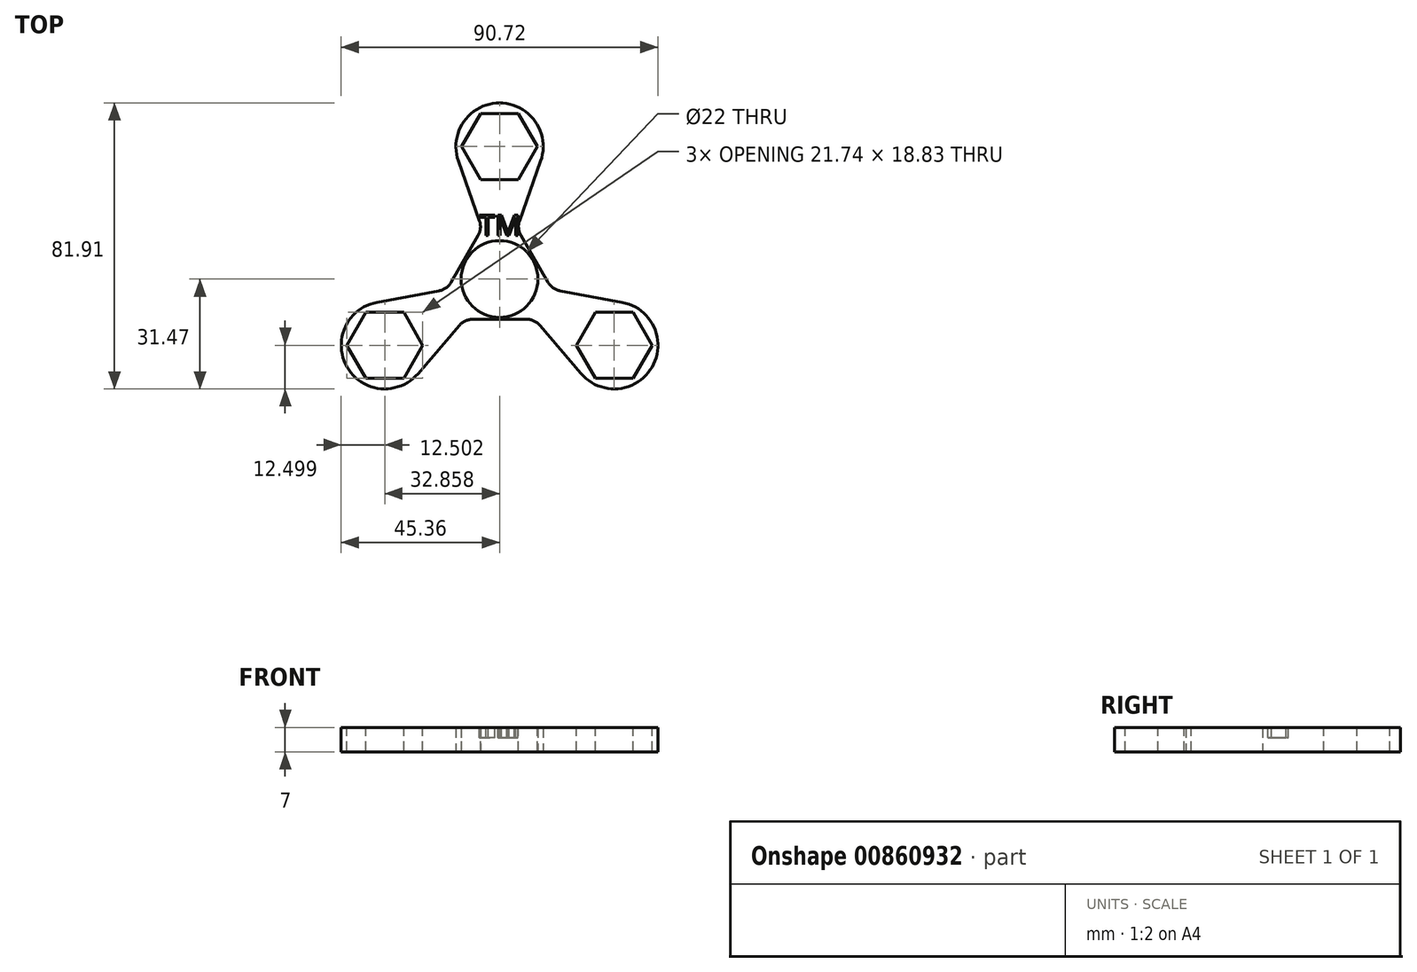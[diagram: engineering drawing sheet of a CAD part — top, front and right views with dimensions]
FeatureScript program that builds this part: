
annotation { "Feature Type Name" : "Feature", "Feature Type Description" : "" }
export const myFeature = defineFeature(function(context is Context, id is Id, definition is map)
    precondition{}
    {
        {
            var Q0;
            Q0=qCreatedBy(makeId("Top.planeOp"),FACE);
            var sketch = newSketch(context, id + "F0", { "sketchPlane" : qUnion([Q0])});
            skCircle(sketch, "E0", {"center": v(0, 0) * mm, "radius": 11 * mm});
            skArc(sketch, "E1", {"start": v(11.78, 33.76) * mm, "mid": v(0.01, 50.44) * mm, "end": v(-11.79, 33.78) * mm});
            skLineSegment(sketch, "E2", {"start": v(-11.79, 33.78) * mm, "end": v(-4.99, 14.5) * mm});
            skLineSegment(sketch, "E3", {"start": v(-4.99, 14.5) * mm, "end": v(-4.99, 14.5) * mm});
            skLineSegment(sketch, "E4", {"start": v(11.78, 33.76) * mm, "end": v(4.94, 14.5) * mm});
            skLineSegment(sketch, "E5", {"start": v(4.94, 14.5) * mm, "end": v(14.88, -2.63) * mm});
            skArc(sketch, "E6.1.0", {"start": v(-35.13, -6.68) * mm, "mid": v(-43.69, -25.2) * mm, "end": v(-23.36, -27.1) * mm});
            skLineSegment(sketch, "E6.1.1", {"start": v(-35.13, -6.68) * mm, "end": v(-15.03, -2.97) * mm});
            skLineSegment(sketch, "E6.1.2", {"start": v(-15.03, -2.97) * mm, "end": v(-4.99, 14.5) * mm});
            skLineSegment(sketch, "E6.1.3", {"start": v(-23.36, -27.1) * mm, "end": v(-10.07, -11.57) * mm});
            skLineSegment(sketch, "E6.1.4", {"start": v(3.35, -11.54) * mm, "end": v(-10.07, -11.57) * mm});
            skArc(sketch, "E6.2.0", {"start": v(23.35, -27.08) * mm, "mid": v(43.68, -25.23) * mm, "end": v(35.15, -6.68) * mm});
            skLineSegment(sketch, "E6.2.1", {"start": v(23.35, -27.08) * mm, "end": v(10.09, -11.53) * mm});
            skLineSegment(sketch, "E6.2.2", {"start": v(10.09, -11.53) * mm, "end": v(3.35, -11.54) * mm});
            skLineSegment(sketch, "E6.2.3", {"start": v(35.15, -6.68) * mm, "end": v(15.05, -2.93) * mm});
            skLineSegment(sketch, "E6.2.4", {"start": v(14.88, -2.63) * mm, "end": v(15.05, -2.93) * mm});
            skPoint(sketch, "E7.orphan", {"position": v(7.92, 9.37) * mm});
            skPoint(sketch, "E8.orphan", {"position": v(15.2, -3.2) * mm});
            skPoint(sketch, "E9.orphan", {"position": v(4.16, -11.54) * mm});
            skCircle(sketch, "E10", {"center": v(0, 0) * mm, "radius": 50.44 * mm, "construction": true});
            skSolve(sketch);
        }
        {
            var Q0;
            Q0=makeQuery(id+"F0.imprint","IMPRINT",FACE,{"disambiguationData":[TD([[makeQuery(id+"F0.imprint","IMPRINT",EDGE,{"derivedFrom":sQuery(id+"F0.wireOp",EDGE,"E0")}),-1.0]])]});
            extrude(context, id + "F1", {"entities" : qUnion([Q0]), "depth" : 7 * mm, "offsetDistance" : 25 * mm});
        }
        {
            var Q0;
            Q0=makeQuery(id+"F1.opExtrude","CAP_FACE",FACE,{"disambiguationData":[OSD([sQuery(id+"F0.wireOp",EDGE,"E0"),sQuery(id+"F0.wireOp",EDGE,"E1"),sQuery(id+"F0.wireOp",EDGE,"E2"),sQuery(id+"F0.wireOp",EDGE,"E3"),sQuery(id+"F0.wireOp",EDGE,"E4"),sQuery(id+"F0.wireOp",EDGE,"E5"),sQuery(id+"F0.wireOp",EDGE,"E6.1.0"),sQuery(id+"F0.wireOp",EDGE,"E6.1.1"),sQuery(id+"F0.wireOp",EDGE,"E6.1.2"),sQuery(id+"F0.wireOp",EDGE,"E6.1.3"),sQuery(id+"F0.wireOp",EDGE,"E6.1.4"),sQuery(id+"F0.wireOp",EDGE,"E6.2.0"),sQuery(id+"F0.wireOp",EDGE,"E6.2.1"),sQuery(id+"F0.wireOp",EDGE,"E6.2.2"),sQuery(id+"F0.wireOp",EDGE,"E6.2.3"),sQuery(id+"F0.wireOp",EDGE,"E6.2.4")])],"isStart":false});
            var sketch = newSketch(context, id + "F2", { "sketchPlane" : qUnion([Q0])});
            skCircle(sketch, "E11.cCircle", {"center": v(0, 37.94) * mm, "radius": 9.41 * mm, "construction": true});
            skLineSegment(sketch, "E11.0", {"start": v(-5.44, 47.36) * mm, "end": v(5.44, 47.36) * mm});
            skLineSegment(sketch, "E11.1", {"start": v(5.44, 47.36) * mm, "end": v(10.87, 37.94) * mm});
            skLineSegment(sketch, "E11.2", {"start": v(10.87, 37.94) * mm, "end": v(5.44, 28.53) * mm});
            skLineSegment(sketch, "E11.3", {"start": v(5.44, 28.53) * mm, "end": v(-5.44, 28.53) * mm});
            skLineSegment(sketch, "E11.4", {"start": v(-5.44, 28.53) * mm, "end": v(-10.87, 37.94) * mm});
            skLineSegment(sketch, "E11.5", {"start": v(-10.87, 37.94) * mm, "end": v(-5.44, 47.36) * mm});
            skPoint(sketch, "E11.0.midPoint", {"position": v(0, 47.36) * mm});
            skLineSegment(sketch, "E12.1.0", {"start": v(-38.3, -28.39) * mm, "end": v(-43.73, -18.97) * mm});
            skLineSegment(sketch, "E12.1.1", {"start": v(-43.73, -18.97) * mm, "end": v(-38.3, -9.56) * mm});
            skLineSegment(sketch, "E12.1.2", {"start": v(-38.3, -9.56) * mm, "end": v(-27.42, -9.56) * mm});
            skLineSegment(sketch, "E12.1.3", {"start": v(-27.42, -9.56) * mm, "end": v(-21.99, -18.97) * mm});
            skLineSegment(sketch, "E12.1.4", {"start": v(-21.99, -18.97) * mm, "end": v(-27.42, -28.39) * mm});
            skLineSegment(sketch, "E12.1.5", {"start": v(-27.42, -28.39) * mm, "end": v(-38.3, -28.39) * mm});
            skLineSegment(sketch, "E12.2.0", {"start": v(43.73, -18.97) * mm, "end": v(38.3, -28.39) * mm});
            skLineSegment(sketch, "E12.2.1", {"start": v(38.3, -28.39) * mm, "end": v(27.42, -28.39) * mm});
            skLineSegment(sketch, "E12.2.2", {"start": v(27.42, -28.39) * mm, "end": v(21.99, -18.97) * mm});
            skLineSegment(sketch, "E12.2.3", {"start": v(21.99, -18.97) * mm, "end": v(27.42, -9.56) * mm});
            skLineSegment(sketch, "E12.2.4", {"start": v(27.42, -9.56) * mm, "end": v(38.3, -9.56) * mm});
            skLineSegment(sketch, "E12.2.5", {"start": v(38.3, -9.56) * mm, "end": v(43.73, -18.97) * mm});
            skPoint(sketch, "E12.center", {"position": v(0, 0) * mm});
            skSolve(sketch);
        }
        {
            var Q0;
            Q0=makeQuery(id+"F2.imprint","IMPRINT",FACE,{"disambiguationData":[TD([[makeQuery(id+"F2.imprint","IMPRINT",EDGE,{"derivedFrom":sQuery(id+"F2.wireOp",EDGE,"E11.0")}),-1.0]])]});
            var Q1;
            Q1=makeQuery(id+"F2.imprint","IMPRINT",FACE,{"disambiguationData":[TD([[makeQuery(id+"F2.imprint","IMPRINT",EDGE,{"derivedFrom":sQuery(id+"F2.wireOp",EDGE,"E12.1.0")}),-1.0]])]});
            var Q2;
            Q2=makeQuery(id+"F2.imprint","IMPRINT",FACE,{"disambiguationData":[TD([[makeQuery(id+"F2.imprint","IMPRINT",EDGE,{"derivedFrom":sQuery(id+"F2.wireOp",EDGE,"E12.2.0")}),-1.0]])]});
            extrude(context, id + "F3", {"entities" : qUnion([Q0, Q1, Q2]), "operationType" : NewBodyOperationType.REMOVE, "oppositeDirection" : true, "depth" : 25 * mm, "offsetDistance" : 25 * mm});
        }
        {
            var Q0;
            Q0=makeQuery(id+"F1.opExtrude","SWEPT_EDGE",EDGE,{"disambiguationData":[OSD([sQuery(id+"F0.wireOp",EDGE,"E6.2.1"),sQuery(id+"F0.wireOp",EDGE,"E6.2.2")])]});
            var Q1;
            Q1=makeQuery(id+"F1.opExtrude","SWEPT_EDGE",EDGE,{"disambiguationData":[OSD([sQuery(id+"F0.wireOp",EDGE,"E6.1.3"),sQuery(id+"F0.wireOp",EDGE,"E6.1.4")])]});
            var Q2;
            Q2=makeQuery(id+"F1.opExtrude","SWEPT_EDGE",EDGE,{"disambiguationData":[OSD([sQuery(id+"F0.wireOp",EDGE,"E5"),sQuery(id+"F0.wireOp",EDGE,"E6.2.3")])]});
            var Q3;
            Q3=makeQuery(id+"F1.opExtrude","SWEPT_EDGE",EDGE,{"disambiguationData":[OSD([sQuery(id+"F0.wireOp",EDGE,"E4"),sQuery(id+"F0.wireOp",EDGE,"E5")])]});
            var Q4;
            Q4=makeQuery(id+"F1.opExtrude","SWEPT_EDGE",EDGE,{"disambiguationData":[OSD([sQuery(id+"F0.wireOp",EDGE,"E6.1.1"),sQuery(id+"F0.wireOp",EDGE,"E6.1.2")])]});
            var Q5;
            Q5=makeQuery(id+"F1.opExtrude","SWEPT_EDGE",EDGE,{"disambiguationData":[OSD([sQuery(id+"F0.wireOp",EDGE,"E2"),sQuery(id+"F0.wireOp",EDGE,"E6.1.2")])]});
            fillet(context, id + "F4", {"entities" : qUnion([Q0, Q1, Q2, Q3, Q4, Q5]), "radius" : 5 * mm, "tangentPropagation" : true, "allowEdgeOverflow" : false});
        }
        {
            var Q0;
            Q0=makeQuery(id+"F1.opExtrude","CAP_FACE",FACE,{"disambiguationData":[OSD([sQuery(id+"F0.wireOp",EDGE,"E0"),sQuery(id+"F0.wireOp",EDGE,"E1"),sQuery(id+"F0.wireOp",EDGE,"E2"),sQuery(id+"F0.wireOp",EDGE,"E4"),sQuery(id+"F0.wireOp",EDGE,"E5"),sQuery(id+"F0.wireOp",EDGE,"E6.1.0"),sQuery(id+"F0.wireOp",EDGE,"E6.1.1"),sQuery(id+"F0.wireOp",EDGE,"E6.1.2"),sQuery(id+"F0.wireOp",EDGE,"E6.1.3"),sQuery(id+"F0.wireOp",EDGE,"E6.1.4"),sQuery(id+"F0.wireOp",EDGE,"E6.2.0"),sQuery(id+"F0.wireOp",EDGE,"E6.2.1"),sQuery(id+"F0.wireOp",EDGE,"E6.2.2"),sQuery(id+"F0.wireOp",EDGE,"E6.2.3")])],"isStart":false});
            var sketch = newSketch(context, id + "F5", { "sketchPlane" : qUnion([Q0])});
            skText(sketch, "E13", { "text": "TM\n", "fontName": "OpenSans-Regular.ttf"});
            const initialGuessF5  = {"E13": [-0.00584, 0.01246, 1, 0, 0.00591]};
            skSetInitialGuess(sketch, initialGuessF5);
            skSolve(sketch);
        }
        {
            var Q0;
            Q0 = qSketchRegion(id + "F5", true);
            extrude(context, id + "F6", {"entities" : qUnion([Q0]), "operationType" : NewBodyOperationType.REMOVE, "oppositeDirection" : true, "depth" : 3 * mm, "offsetDistance" : 25 * mm});
        }
    });
